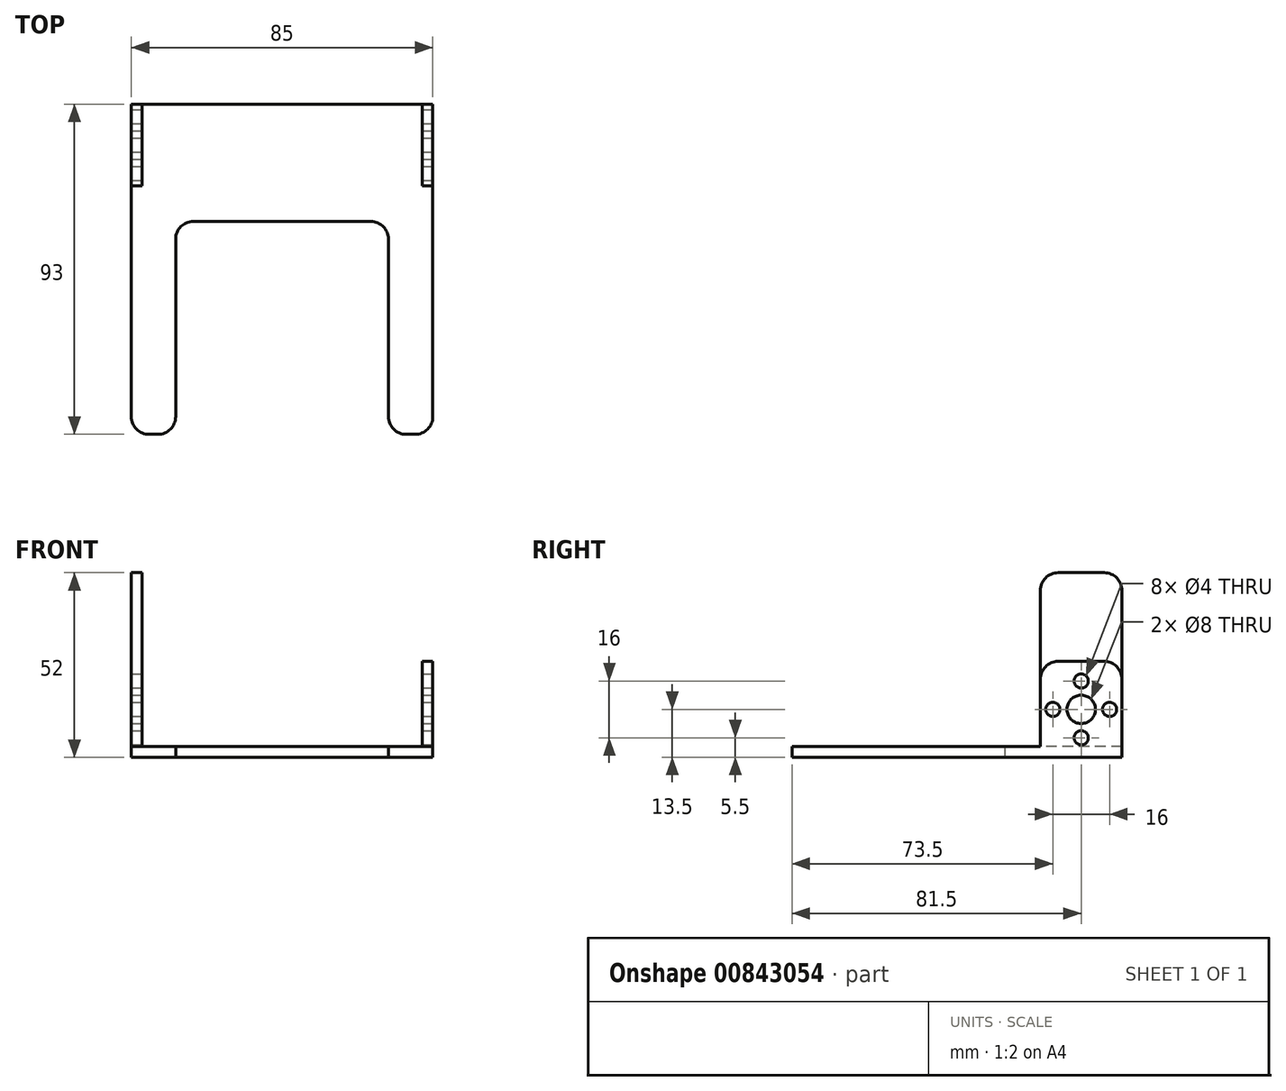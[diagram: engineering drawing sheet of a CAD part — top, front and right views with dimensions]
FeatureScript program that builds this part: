
annotation { "Feature Type Name" : "Feature", "Feature Type Description" : "" }
export const myFeature = defineFeature(function(context is Context, id is Id, definition is map)
    precondition{}
    {
        {
            var Q0;
            Q0=qCreatedBy(makeId("Top.planeOp"),FACE);
            var sketch = newSketch(context, id + "F0", { "sketchPlane" : qUnion([Q0])});
            skLineSegment(sketch, "E0.bottom", {"start": v(0, 0) * mm, "end": v(85, 0) * mm});
            skLineSegment(sketch, "E0.top", {"start": v(0, 23) * mm, "end": v(85, 23) * mm});
            skLineSegment(sketch, "E0.left", {"start": v(0, 0) * mm, "end": v(0, 23) * mm});
            skLineSegment(sketch, "E0.right", {"start": v(85, 0) * mm, "end": v(85, 23) * mm});
            skLineSegment(sketch, "E1.top", {"start": v(17.5, -10) * mm, "end": v(67.5, -10) * mm});
            skLineSegment(sketch, "E1.left", {"start": v(0, 0) * mm, "end": v(0, -10) * mm});
            skLineSegment(sketch, "E1.right", {"start": v(85, 0) * mm, "end": v(85, -10) * mm});
            skLineSegment(sketch, "E2.top", {"start": v(5, -70) * mm, "end": v(7.5, -70) * mm});
            skLineSegment(sketch, "E2.left", {"start": v(0, -10) * mm, "end": v(0, -65) * mm});
            skLineSegment(sketch, "E2.right", {"start": v(12.5, -15) * mm, "end": v(12.5, -65) * mm});
            skLineSegment(sketch, "E3.top", {"start": v(80, -70) * mm, "end": v(77.5, -70) * mm});
            skLineSegment(sketch, "E3.left", {"start": v(85, -10) * mm, "end": v(85, -65) * mm});
            skLineSegment(sketch, "E3.right", {"start": v(72.5, -15) * mm, "end": v(72.5, -65) * mm});
            skPoint(sketch, "E4.visualSharp", {"position": v(12.5, -70) * mm});
            skArc(sketch, "E4.filletArc", {"start": v(7.5, -70) * mm, "mid": v(11.04, -68.54) * mm, "end": v(12.5, -65) * mm});
            skPoint(sketch, "E5.visualSharp", {"position": v(0, -70) * mm});
            skArc(sketch, "E5.filletArc", {"start": v(0, -65) * mm, "mid": v(1.46, -68.54) * mm, "end": v(5, -70) * mm});
            skPoint(sketch, "E6.visualSharp", {"position": v(72.5, -70) * mm});
            skArc(sketch, "E6.filletArc", {"start": v(72.5, -65) * mm, "mid": v(73.96, -68.54) * mm, "end": v(77.5, -70) * mm});
            skPoint(sketch, "E7.visualSharp", {"position": v(85, -70) * mm});
            skArc(sketch, "E7.filletArc", {"start": v(80, -70) * mm, "mid": v(83.54, -68.54) * mm, "end": v(85, -65) * mm});
            skPoint(sketch, "E8.visualSharp", {"position": v(12.5, -10) * mm});
            skArc(sketch, "E8.filletArc", {"start": v(17.5, -10) * mm, "mid": v(13.96, -11.46) * mm, "end": v(12.5, -15) * mm});
            skPoint(sketch, "E9.visualSharp", {"position": v(72.5, -10) * mm});
            skArc(sketch, "E9.filletArc", {"start": v(72.5, -15) * mm, "mid": v(71.04, -11.46) * mm, "end": v(67.5, -10) * mm});
            skSolve(sketch);
        }
        {
            var Q0;
            Q0=qSketchRegion(id+"F0",true);
            extrude(context, id + "F1", {"entities" : qUnion([Q0]), "depth" : 3 * mm, "offsetDistance" : 25 * mm});
        }
        {
            var Q0;
            Q0=makeQuery(id+"F1.opExtrude","CAP_FACE",FACE,{"disambiguationData":[OSD([sQuery(id+"F0.wireOp",EDGE,"E0.bottom"),sQuery(id+"F0.wireOp",EDGE,"E0.top"),sQuery(id+"F0.wireOp",EDGE,"E0.left"),sQuery(id+"F0.wireOp",EDGE,"E0.right")])],"isStart":false});
            var sketch = newSketch(context, id + "F2", { "sketchPlane" : qUnion([Q0])});
            skLineSegment(sketch, "E10.bottom", {"start": v(0, 23) * mm, "end": v(3, 23) * mm});
            skLineSegment(sketch, "E10.top", {"start": v(0, 0) * mm, "end": v(3, 0) * mm});
            skLineSegment(sketch, "E10.left", {"start": v(0, 23) * mm, "end": v(0, 0) * mm});
            skLineSegment(sketch, "E10.right", {"start": v(3, 23) * mm, "end": v(3, 0) * mm});
            skLineSegment(sketch, "E11.bottom", {"start": v(85, 23) * mm, "end": v(82, 23) * mm});
            skLineSegment(sketch, "E11.top", {"start": v(85, 0) * mm, "end": v(82, 0) * mm});
            skLineSegment(sketch, "E11.left", {"start": v(85, 23) * mm, "end": v(85, 0) * mm});
            skLineSegment(sketch, "E11.right", {"start": v(82, 23) * mm, "end": v(82, 0) * mm});
            skSolve(sketch);
        }
        {
            var Q0;
            Q0=qSketchRegion(id+"F2",true);
            extrude(context, id + "F3", {"entities" : qUnion([Q0]), "operationType" : NewBodyOperationType.ADD, "depth" : 24 * mm, "offsetDistance" : 25 * mm});
        }
        {
            var Q0;
            Q0=makeQuery(id+"F3.opExtrude","CAP_FACE",FACE,{"disambiguationData":[OSD([sQuery(id+"F2.wireOp",EDGE,"E10.bottom"),sQuery(id+"F2.wireOp",EDGE,"E10.top"),sQuery(id+"F2.wireOp",EDGE,"E10.left"),sQuery(id+"F2.wireOp",EDGE,"E10.right")])],"isStart":false});
            var sketch = newSketch(context, id + "F4", { "sketchPlane" : qUnion([Q0])});
            skLineSegment(sketch, "E12.bottom", {"start": v(0, 23) * mm, "end": v(3, 23) * mm});
            skLineSegment(sketch, "E12.top", {"start": v(0, 0) * mm, "end": v(3, 0) * mm});
            skLineSegment(sketch, "E12.left", {"start": v(0, 23) * mm, "end": v(0, 0) * mm});
            skLineSegment(sketch, "E12.right", {"start": v(3, 23) * mm, "end": v(3, 0) * mm});
            skSolve(sketch);
        }
        {
            var Q0;
            Q0=qSketchRegion(id+"F4",true);
            extrude(context, id + "F5", {"entities" : qUnion([Q0]), "operationType" : NewBodyOperationType.ADD, "depth" : 25 * mm, "offsetDistance" : 25 * mm});
        }
        {
            var Q0;
            Q0=makeQuery(id+"F3.boolean.opBoolean","MERGE",FACE,{"derivedFrom":[makeQuery(id+"F1.opExtrude","SWEPT_FACE",FACE,{"disambiguationData":[OSD([sQuery(id+"F0.wireOp",EDGE,"E0.right"),sQuery(id+"F0.wireOp",EDGE,"E1.right"),sQuery(id+"F0.wireOp",EDGE,"E3.left")])]}),makeQuery(id+"F3.opExtrude","SWEPT_FACE",FACE,{"disambiguationData":[OSD([sQuery(id+"F2.wireOp",EDGE,"E11.left")])]})]});
            var sketch = newSketch(context, id + "F6", { "sketchPlane" : qUnion([Q0])});
            skLineSegment(sketch, "E13", {"start": v(0, 27) * mm, "end": v(23, 0) * mm, "construction": true});
            skLineSegment(sketch, "E14", {"start": v(23, 27) * mm, "end": v(0, 0) * mm, "construction": true});
            skCircle(sketch, "E15", {"center": v(11.5, 13.5) * mm, "radius": 4 * mm});
            skCircle(sketch, "E16", {"center": v(19.5, 13.5) * mm, "radius": 2 * mm});
            skCircle(sketch, "E17.1.0", {"center": v(11.5, 21.5) * mm, "radius": 2 * mm});
            skCircle(sketch, "E17.2.0", {"center": v(3.5, 13.5) * mm, "radius": 2 * mm});
            skCircle(sketch, "E17.3.0", {"center": v(11.5, 5.5) * mm, "radius": 2 * mm});
            skSolve(sketch);
        }
        {
            var Q0;
            Q0 = qSketchRegion(id + "F6", true);
            extrude(context, id + "F7", {"entities" : qUnion([Q0]), "operationType" : NewBodyOperationType.REMOVE, "oppositeDirection" : true, "depth" : 100 * mm, "offsetDistance" : 25 * mm});
        }
        {
            var Q0;
            Q0=makeQuery(id+"F3.opExtrude","CAP_EDGE",EDGE,{"disambiguationData":[OSD([sQuery(id+"F2.wireOp",EDGE,"E11.top")])],"isStart":false});
            var Q1;
            Q1=makeQuery(id+"F3.opExtrude","CAP_EDGE",EDGE,{"disambiguationData":[OSD([sQuery(id+"F2.wireOp",EDGE,"E11.bottom")])],"isStart":false});
            var Q2;
            Q2=makeQuery(id+"F5.opExtrude","CAP_EDGE",EDGE,{"disambiguationData":[OSD([sQuery(id+"F4.wireOp",EDGE,"E12.bottom")])],"isStart":false});
            var Q3;
            Q3=makeQuery(id+"F5.opExtrude","CAP_EDGE",EDGE,{"disambiguationData":[OSD([sQuery(id+"F4.wireOp",EDGE,"E12.top")])],"isStart":false});
            fillet(context, id + "F8", {"entities" : qUnion([Q0, Q1, Q2, Q3]), "radius" : 5 * mm, "tangentPropagation" : true, "allowEdgeOverflow" : false});
        }
    });
